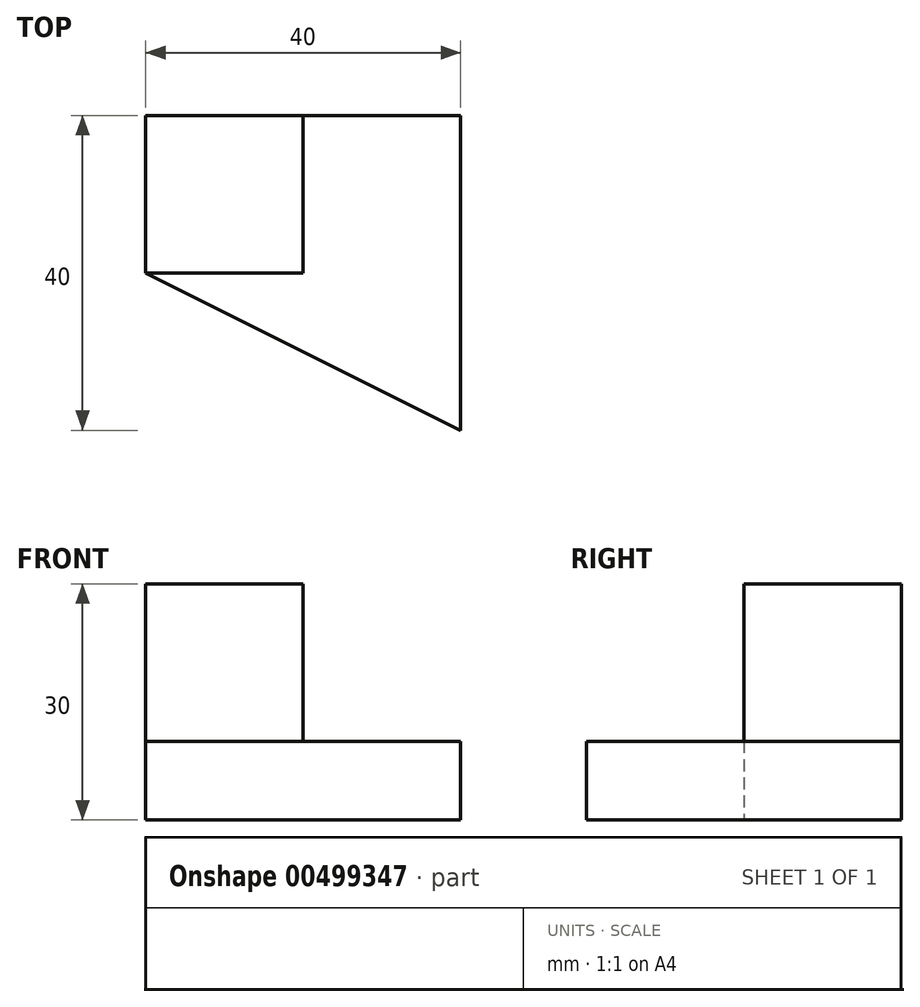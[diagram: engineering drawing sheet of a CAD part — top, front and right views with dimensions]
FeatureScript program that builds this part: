
annotation { "Feature Type Name" : "Feature", "Feature Type Description" : "" }
export const myFeature = defineFeature(function(context is Context, id is Id, definition is map)
    precondition{}
    {
        {
            var Q0;
            Q0=qCreatedBy(makeId("Top.planeOp"),FACE);
            var sketch = newSketch(context, id + "F0", { "sketchPlane" : qUnion([Q0])});
            skLineSegment(sketch, "E0", {"start": v(0, 0) * mm, "end": v(0, 20) * mm});
            skLineSegment(sketch, "E1", {"start": v(0, 20) * mm, "end": v(40, 20) * mm});
            skLineSegment(sketch, "E2", {"start": v(40, 20) * mm, "end": v(40, -20) * mm});
            skLineSegment(sketch, "E3", {"start": v(0, 0) * mm, "end": v(40, -20) * mm});
            skSolve(sketch);
        }
        {
            var Q0;
            Q0 = qSketchRegion(id + "F0", true);
            extrude(context, id + "F1", {"entities" : qUnion([Q0]), "depth" : 10 * mm});
        }
        {
            var Q0;
            Q0=makeQuery(id+"F1.opExtrude","CAP_FACE",FACE,{"disambiguationData":[OSD([sQuery(id+"F0.wireOp",EDGE,"E0"),sQuery(id+"F0.wireOp",EDGE,"E1"),sQuery(id+"F0.wireOp",EDGE,"E2"),sQuery(id+"F0.wireOp",EDGE,"E3")])],"isStart":false});
            var sketch = newSketch(context, id + "F2", { "sketchPlane" : qUnion([Q0])});
            skLineSegment(sketch, "E4.bottom", {"start": v(0, 20) * mm, "end": v(20, 20) * mm});
            skLineSegment(sketch, "E4.top", {"start": v(0, 0) * mm, "end": v(20, 0) * mm});
            skLineSegment(sketch, "E4.left", {"start": v(0, 20) * mm, "end": v(0, 0) * mm});
            skLineSegment(sketch, "E4.right", {"start": v(20, 20) * mm, "end": v(20, 0) * mm});
            skSolve(sketch);
        }
        {
            var Q0;
            Q0 = qSketchRegion(id + "F2", true);
            extrude(context, id + "F3", {"entities" : qUnion([Q0]), "operationType" : NewBodyOperationType.ADD, "depth" : (20) * mm});
        }
    });
